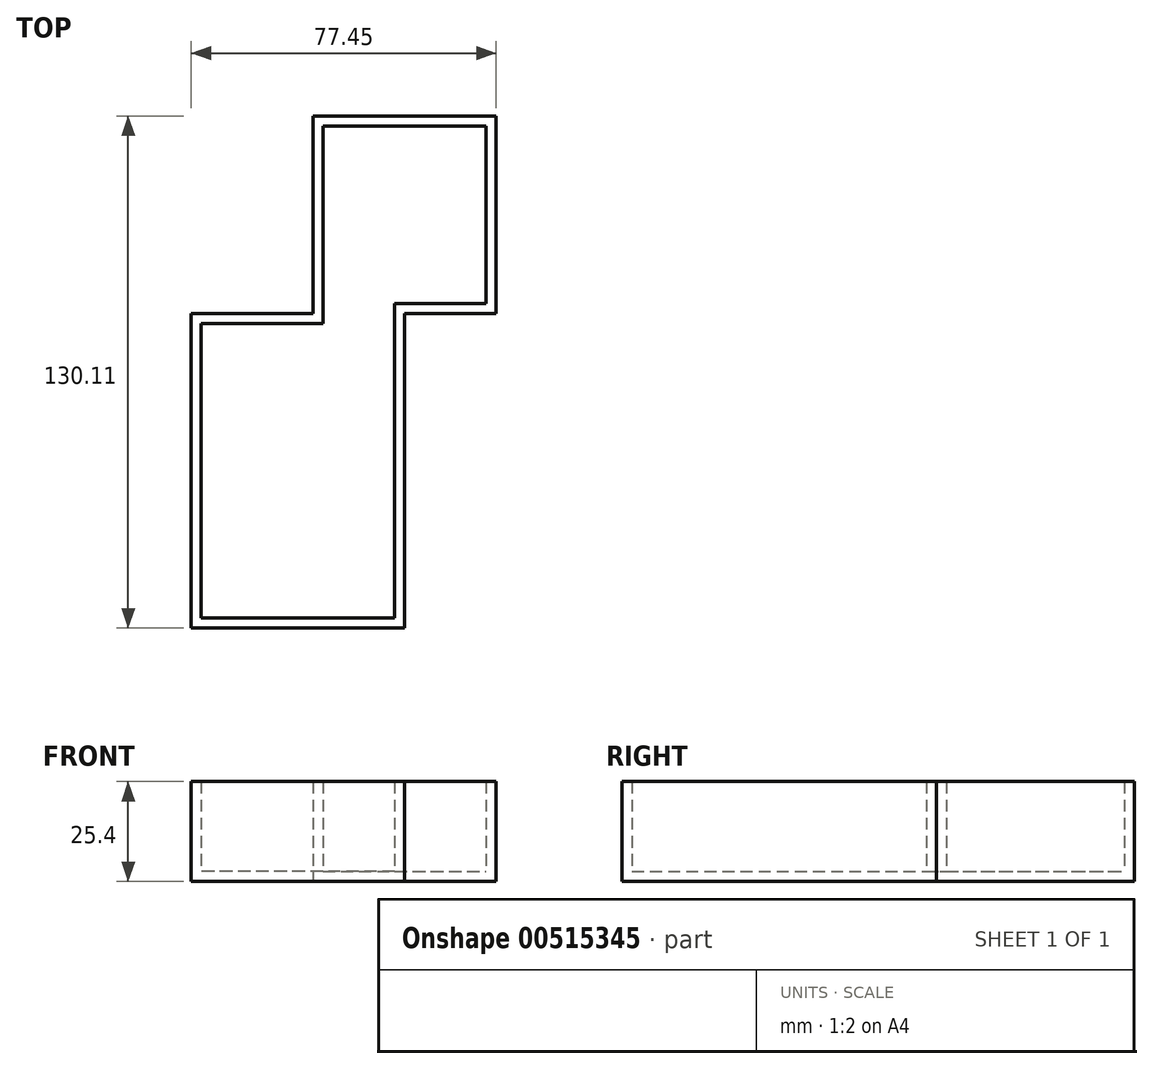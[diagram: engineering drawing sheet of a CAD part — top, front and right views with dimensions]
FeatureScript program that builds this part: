
annotation { "Feature Type Name" : "Feature", "Feature Type Description" : "" }
export const myFeature = defineFeature(function(context is Context, id is Id, definition is map)
    precondition{}
    {
        {
            var Q0;
            Q0=qCreatedBy(makeId("Top.planeOp"),FACE);
            var sketch = newSketch(context, id + "F0", { "sketchPlane" : qUnion([Q0])});
            skLineSegment(sketch, "E0.bottom", {"start": v(0, 79.93) * mm, "end": v(46.5, 79.93) * mm});
            skLineSegment(sketch, "E0.top", {"start": v(0, 130.11) * mm, "end": v(46.5, 130.11) * mm});
            skLineSegment(sketch, "E0.left", {"start": v(0, 79.93) * mm, "end": v(0, 130.11) * mm});
            skLineSegment(sketch, "E0.right", {"start": v(46.5, 79.93) * mm, "end": v(46.5, 130.11) * mm});
            skPoint(sketch, "E1.firstSnap0", {"position": v(23.25, 79.93) * mm});
            skLineSegment(sketch, "E1.bottom", {"start": v(23.25, 0) * mm, "end": v(-30.95, 0) * mm});
            skLineSegment(sketch, "E1.top", {"start": v(23.25, 79.93) * mm, "end": v(-30.95, 79.93) * mm});
            skLineSegment(sketch, "E1.left", {"start": v(23.25, 0) * mm, "end": v(23.25, 79.93) * mm});
            skLineSegment(sketch, "E1.right", {"start": v(-30.95, 0) * mm, "end": v(-30.95, 79.93) * mm});
            skSolve(sketch);
        }
        {
            var Q0;
            Q0 = qSketchRegion(id + "F0", true);
            extrude(context, id + "F1", {"entities" : qUnion([Q0]), "depth" : 25.4 * mm, "offsetDistance" : 25.4 * mm});
        }
        {
            var Q0;
            Q0=makeQuery(id+"F1.opExtrude","CAP_FACE",FACE,{"disambiguationData":[OSD([sQuery(id+"F0.wireOp",EDGE,"E0.bottom"),sQuery(id+"F0.wireOp",EDGE,"E0.top"),sQuery(id+"F0.wireOp",EDGE,"E0.left"),sQuery(id+"F0.wireOp",EDGE,"E0.right"),sQuery(id+"F0.wireOp",EDGE,"E1.bottom"),sQuery(id+"F0.wireOp",EDGE,"E1.top"),sQuery(id+"F0.wireOp",EDGE,"E1.left"),sQuery(id+"F0.wireOp",EDGE,"E1.right")])],"isStart":false});
            shell(context, id + "F2", {"entities" : qUnion([Q0]), "thickness" : 2.54 * mm});
        }
    });
